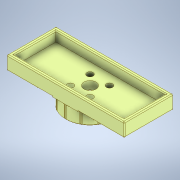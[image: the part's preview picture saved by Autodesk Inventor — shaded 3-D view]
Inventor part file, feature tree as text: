
AUTODESK INVENTOR PART (.ipt)
format: ipt  version: 2022 (Build 260153000, 153)  size: 460,800 bytes
history: native  units: mm
features: sketch x8, extrude x7, fillet x3, other x2, pattern_circular x1, revolve x1, projected_geometry x1
ambient origin geometry x8: Origin, YZ Plane, XZ Plane, XY Plane, X Axis, Y Axis, Z Axis, Center Point
bodies: Body1 (feature_tree)
feature tree (23):
  other  "Твердое тело1"
  extrude  "Выдавливание1"  Depth=20.0mm
  extrude  "Выдавливание2"  Depth=55.6mm
  sketch  "Эскиз3"
  extrude  "Выдавливание3"  Depth=2.5mm
  extrude  "Выдавливание4"  Depth=2.0mm
  sketch  "Эскиз6"
  extrude  "Выдавливание5"  Depth=2.0mm TaperAngle=0.0deg
  extrude  "Выдавливание6"  Depth=2.0mm
  extrude  "Выдавливание7"  Depth=2.0mm
  fillet  "Сопряжение2"  Radius=5.0mm
  pattern_circular  "Круговой массив1"  [2 undecoded]
  fillet  "Сопряжение3"  Radius=40.0mm
  other  "РабПлоскость1"
  revolve  "Вращение1"
  fillet  "Сопряжение4"  Radius=3.2mm
  sketch  "Эскиз1"
  sketch  "Эскиз2"
  projected_geometry  "Спроецированная петля1"
  sketch  "Эскиз4"
  sketch  "Эскиз7"
  sketch  "Эскиз8"
  sketch  "Эскиз10"
note: 2 required parameter values undecoded (feature->parameter linkage not recoverable at this tier; creation-order binding heuristic only, values carry confidence <= 0.55)
